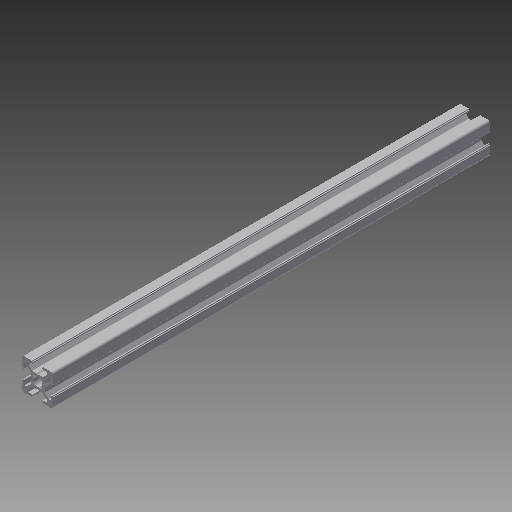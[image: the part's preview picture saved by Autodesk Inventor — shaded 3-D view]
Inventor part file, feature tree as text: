
AUTODESK INVENTOR PART (.ipt)
format: ipt  version: 2017 (Build 210142000, 142)  size: 310,784 bytes
history: native  units: in
note: dims shown in document units (in); Inventor stores cm internally (conversion verified against a paired STEP export)
features: other x3, extrude x1, sketch x1
ambient origin geometry x8: Origin, YZ Plane, XZ Plane, XY Plane, X Axis, Y Axis, Z Axis, Center Point
bodies: Solid1 (feature_tree)
feature tree (5):
  other  "Blocks"
  extrude  "Extrusion1"  Depth=1.0in
  sketch  "Sketch1"  dims[d1=0.0in d13=1.0in d14=1.0in]
  other  "20x20"
  other  "20x20:1"
